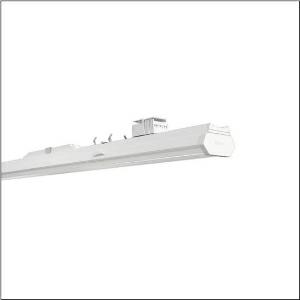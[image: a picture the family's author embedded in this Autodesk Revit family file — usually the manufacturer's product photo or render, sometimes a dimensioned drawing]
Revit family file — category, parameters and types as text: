
# Revit family: licross_r__11_protected_ho_51ts12cn4c5l_6297
name_source: partatom
category: Lighting Fixtures
units: mm (PartAtom-declared; Revit-internal decimal feet)

## family parameters
Cut with Voids When Loaded = No
Host = Face
Light Source = No
Part Type = Normal
Room Calculation Point = No
Round Connector Dimension = Use Diameter
Shared = No

## types (1)
- --- (1 x LED, 12600 lm, 78.7 W, 4000K)
    Apparent Load = 79 VA
    CIE Flux Codes = 54 82 95 97 100
    Color Rendering = 80
    Color Temperature = 4000K
    Default Elevation = 1800 mm
    Description = Licross® 11 Protected HOluminaire insert, length: 1.500mm, width: 90mm, height: 101mm, LED rated luminous flux: 12.600lm, light colour: 840, control gear: ON/OFF Multilumen, CLOi, control gear: ECG Multilumen, with plug, 3-pole, with phase selection, mains connection: 220..240V, AC, 50/60Hz, halogen-free wiring, primary optical cover: cover, of PMMA, light emission: direct with ceiling illumination distribution, protection rating (complete): IP50, insulation class (complete): insulation class I (protective earthing), certification: CE, ENEC, VDE, protection symbol: D if used in an environment with non-conductive dust loads with corresponding accessories, permissible ambient temperature for indoor applications: -35..+40°C, reducing of maximum allowable ambient temperature of 5°C with ceiling mounting, corresponds to IFS (International Featured Standards) requirements for safety and quality in the food industry, packaging unit: 1 piece
    Height = 92 mm
    Lamp = 1 x LED
    Lamp Light Flux = 12600 lm
    Lamp Power = 78.7 W
    Lamp count = 1
    Length = 1500 mm
    Luminous efficacy = 160 lm/W
    Manufacturer = Siteco
    ModVariant = No
    Model = 51TS12CN4C5L
    Mounting Place = Ceiling
    Mounting Type = Pendant
    Number of Poles = 1
    OnlyDefault = Yes
    Power Factor = 1
    Product Name = Licross® 11 Protected HO
    Product group = luminaire insert
    ProductGroupID = 902
    Protection Class = Protection class I
    Protection Degree = IP 50
    RLX_Detail_Level = 1
    RlxData = <blob elided: 21805 chars, md5=ba18f0b6>
    Socket = socket
    Standby Power = 0 W
    System Light Flux = 12600 lm
    System Power = 79 W
    Type Comments = factory setting: luminous flux: 100 % | (A | C | E) | 182 mA
    Type Image = l_1256145.jpg
    URL = http://relux.com
    VarID = @adj_138325
    Voltage = 0 V
    Weight = 0.00 kg
    Width = 88 mm

## geometry (parser evidence)
native form markers: Blend x4, Sweep x12
no freeform markers — native parametric forms only
